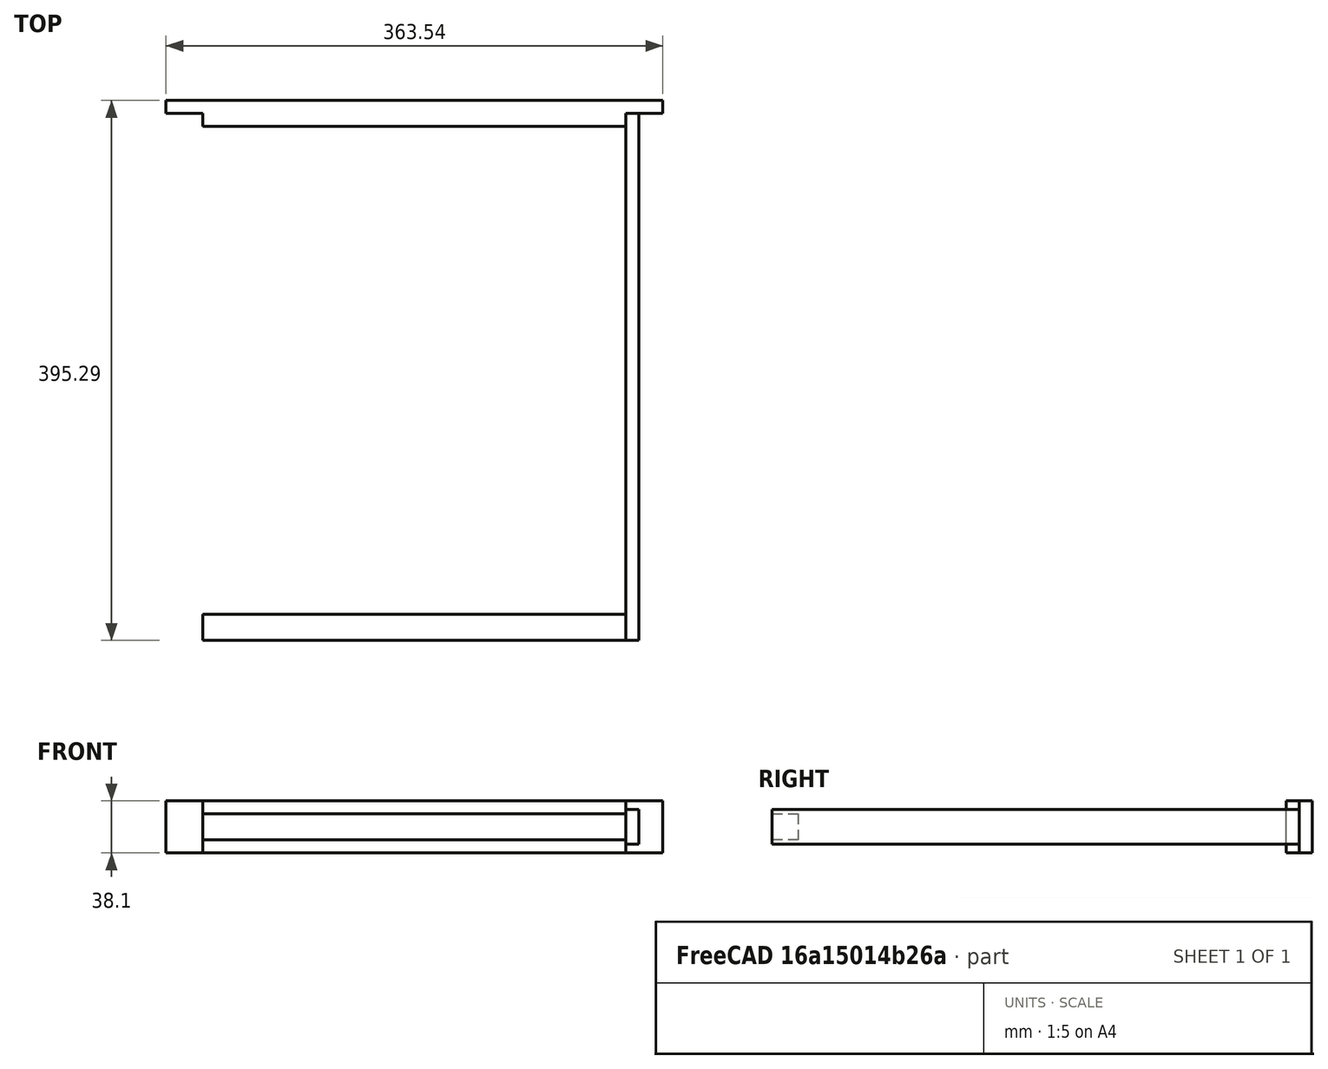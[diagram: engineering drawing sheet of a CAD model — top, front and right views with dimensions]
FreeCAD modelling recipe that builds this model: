
FCSTD DOCUMENT  (FreeCAD 0.19R24366 (Git))
Label: layens-frame
License: Creative Commons Attribution-ShareAlike
LicenseURL: http://creativecommons.org/licenses/by-sa/4.0/
objects: TechDraw::DrawViewDimension×14, TechDraw::DrawProjGroupItem×5, PartDesign::Pad×4, PartDesign::Body×4, Sketcher::SketchObject×3, PartDesign::ShapeBinder×2, App::DocumentObjectGroup×2, TechDraw::DrawSVGTemplate×1, PartDesign::FeatureBase×1, TechDraw::DrawProjGroup×1, TechDraw::DrawViewAnnotation×1, TechDraw::DrawPage×1
note: 18 computed .brp shape members not serialized (recipe doc carries the construction recipe); baked Part::Feature solids carry a one-line shape summary decoded from their .brp
EXTERNAL_REF file=layens-data.FCStd obj=Spreadsheet

FEATURE [Sketcher::SketchObject] Sketch  label="top-bar-sketch"
  FullyConstrained = true
  MapMode = 5
  Support = -> [XY_Plane]
  expr: Constraints[19] = <<layens-data>>#Spreadsheet.frame_topbar_x
  expr: Constraints[21] = <<layens-data>>#Spreadsheet.frame_topbar_z
  expr: Constraints[20] = <<layens-data>>#Spreadsheet.frame_topbar_z / 2
  sketch-geometry (8):
    g0: LineSegment StartX=-181.77 StartY=9.525 StartZ=0 EndX=-181.77 EndY=19.05 EndZ=0
    g1: LineSegment StartX=-181.77 StartY=19.05 StartZ=0 EndX=181.77 EndY=19.05 EndZ=0
    g2: LineSegment StartX=181.77 StartY=19.05 StartZ=0 EndX=181.77 EndY=9.525 EndZ=0
    g3: LineSegment StartX=181.77 StartY=9.525 StartZ=0 EndX=154.782 EndY=9.525 EndZ=0
    g4: LineSegment StartX=154.782 StartY=9.525 StartZ=0 EndX=154.782 EndY=0 EndZ=0
    g5: LineSegment StartX=154.782 StartY=0 StartZ=0 EndX=-154.782 EndY=0 EndZ=0
    g6: LineSegment StartX=-154.782 StartY=0 StartZ=0 EndX=-154.782 EndY=9.525 EndZ=0
    g7: LineSegment StartX=-154.782 StartY=9.525 StartZ=0 EndX=-181.77 EndY=9.525 EndZ=0
  constraints (23):
    c: Vertical(g0)
    c: Coincident(g0,g1)
    c: Coincident(g1,g2)
    c: Vertical(g2)
    c: Coincident(g2,g3)
    c: Horizontal(g3)
    c: Coincident(g3,g4)
    c: PointOnObject(g4,g-1)
    c: Vertical(g4)
    c: Coincident(g5,g6)
    c: Horizontal(g5)
    c: Vertical(g6)
    c: Symmetric(g0,g1,g-2)
    c: Coincident(g7,g0)
    c: Horizontal(g7)
    c: Equal(g7,g3)
    c: Coincident(g6,g7)
    c: Coincident(g5,g4)
    c: Equal(g6,g4)
    c: DistanceX(g1,g1) = 363.54
    c: DistanceY(g6,g6) = 9.525
    c: DistanceY(g5,g0) = 19.05
    c: DistanceX(g7,g7) = 26.9875
FEATURE [PartDesign::Pad] Pad  label="top-bar-pad"
  Direction = (0,0,1)
  Length = 38.1
  Length2 = 100.08
  Midplane = true
  Profile = -> Sketch
  Type = 0
  expr: Length = <<layens-data>>#Spreadsheet.frame_topbar_y
FEATURE [PartDesign::Body] Body  label="top-bar"
  Group = -> [Sketch,Pad]
  Origin = -> Origin
  Tip = -> Pad
FEATURE [PartDesign::ShapeBinder] ShapeBinder
  Support = -> [Pad]
  TraceSupport = false
FEATURE [Sketcher::SketchObject] Sketch001  label="left-bar-sketch"
  ExternalGeometry = -> [ShapeBinder]
  FullyConstrained = true
  MapMode = 5
  Placement = pos=(-154.782,0,0) rot=(0.57735,-0.57735,-0.57735;2.0944rad)
  Support = -> [ShapeBinder]
  expr: Constraints[10] = <<layens-data>>#Spreadsheet.frame_side_x
  expr: Constraints[9] = <<layens-data>>#Spreadsheet.frame_side_y
  sketch-geometry (4):
    g0: LineSegment StartX=-9.525 StartY=12.7 StartZ=0 EndX=376.235 EndY=12.7 EndZ=0
    g1: LineSegment StartX=376.235 StartY=12.7 StartZ=0 EndX=376.235 EndY=-12.7 EndZ=0
    g2: LineSegment StartX=376.235 StartY=-12.7 StartZ=0 EndX=-9.525 EndY=-12.7 EndZ=0
    g3: LineSegment StartX=-9.525 StartY=-12.7 StartZ=0 EndX=-9.525 EndY=12.7 EndZ=0
  constraints (11):
    c: Coincident(g0,g1)
    c: Coincident(g1,g2)
    c: Coincident(g2,g3)
    c: Coincident(g3,g0)
    c: Horizontal(g0)
    c: Horizontal(g2)
    c: Vertical(g1)
    c: PointOnObject(g0,g-3)
    c: Symmetric(g2,g0,g-1)
    c: DistanceX(g2,g2) = 385.76
    c: DistanceY(g3,g3) = 25.4
FEATURE [PartDesign::Pad] Pad001
  Direction = (1,1,1)
  Length = 9.525
  Length2 = 100.076
  Profile = -> Sketch001
  Type = 0
FEATURE [PartDesign::Pad] Pad002  label="left-bar-pad"
  BaseFeature = -> Pad001
  Direction = (1,1,1)
  Length = 9.53
  Length2 = 100.08
  Profile = -> Sketch001
  Type = 0
  expr: Length = <<layens-data>>#Spreadsheet.frame_side_z
FEATURE [PartDesign::Body] Body001  label="left-bar"
  Group = -> [ShapeBinder,Sketch001,Pad001,Pad002]
  Origin = -> Origin001
  Tip = -> Pad002
FEATURE [PartDesign::ShapeBinder] ShapeBinder002
  Support = -> [Pad002]
  TraceSupport = false
FEATURE [Sketcher::SketchObject] Sketch004  label="bottom-bar-sketch"
  ExternalGeometry = -> [ShapeBinder002]
  FullyConstrained = true
  MapMode = 5
  Placement = pos=(-154.782,0,0) rot=(0.57735,0.57735,0.57735;2.0944rad)
  Support = -> [ShapeBinder002]
  expr: Constraints[9] = <<layens-data>>#Spreadsheet.bottom_bar_z
  expr: Constraints[8] = <<layens-data>>#Spreadsheet.bottom_bar_y
  sketch-geometry (4):
    g0: LineSegment StartX=-376.235 StartY=9.525 StartZ=0 EndX=-357.185 EndY=9.525 EndZ=0
    g1: LineSegment StartX=-357.185 StartY=9.525 StartZ=0 EndX=-357.185 EndY=-9.525 EndZ=0
    g2: LineSegment StartX=-357.185 StartY=-9.525 StartZ=0 EndX=-376.235 EndY=-9.525 EndZ=0
    g3: LineSegment StartX=-376.235 StartY=-9.525 StartZ=0 EndX=-376.235 EndY=9.525 EndZ=0
  constraints (11):
    c: Coincident(g0,g1)
    c: Coincident(g1,g2)
    c: Coincident(g2,g3)
    c: Coincident(g3,g0)
    c: Horizontal(g0)
    c: Horizontal(g2)
    c: Vertical(g1)
    c: PointOnObject(g0,g-4)
    c: DistanceX(g0,g0) = 19.05
    c: DistanceY(g1,g1) = 19.05
    c: Symmetric(g0,g2,g-1)
FEATURE [PartDesign::Pad] Pad006  label="bottom-bar-pad"
  Direction = (1,1,1)
  Length = 309.56
  Length2 = 100.08
  Profile = -> Sketch004
  Type = 0
  expr: Length = <<layens-data>>#Spreadsheet.bottom_bar_x
FEATURE [PartDesign::Body] Body004  label="bottom-bar"
  Group = -> [ShapeBinder002,Sketch004,Pad006]
  Origin = -> Origin004
  Tip = -> Pad006
FEATURE [TechDraw::DrawSVGTemplate] Template
  EditableTexts = Designed_by_Name=T.GREENWOOD; Drawing_number=LAYENS-001; FC-Date=AUG 08, 2022; FC-SC=1:6; FC-SH=01; FC-Title=Layens Frame; Subtitle=Simplified Layens Frame; Weight=Weight
  Height = 210
  Orientation = 1
  Width = 297
FEATURE [TechDraw::DrawViewDimension] Dimension002
  Arbitrary = false
  ArbitraryTolerances = false
  EqualTolerance = true
  FormatSpec = %.1f
  FormatSpecOverTolerance = %+.1f
  FormatSpecUnderTolerance = %+.1f
  Inverted = false
  LockPosition = false
  MeasureType = 1
  OverTolerance = 0
  Rotation = 0
  ScaleType = 1
  TheoreticalExact = false
  Type = 1
  UnderTolerance = 0
  X = -0.67029
  Y = 29.7806
FEATURE [TechDraw::DrawViewDimension] Dimension003
  Arbitrary = false
  ArbitraryTolerances = false
  EqualTolerance = true
  FormatSpec = %.1f
  FormatSpecOverTolerance = %+.1f
  FormatSpecUnderTolerance = %+.1f
  Inverted = false
  LockPosition = false
  MeasureType = 1
  OverTolerance = 0
  Rotation = 0
  ScaleType = 1
  TheoreticalExact = false
  Type = 2
  UnderTolerance = 0
  X = 25.2827
  Y = 23.1248
FEATURE [TechDraw::DrawViewDimension] Dimension004
  Arbitrary = false
  ArbitraryTolerances = false
  EqualTolerance = true
  FormatSpec = %.1f
  FormatSpecOverTolerance = %+.1f
  FormatSpecUnderTolerance = %+.1f
  Inverted = false
  LockPosition = false
  MeasureType = 1
  OverTolerance = 0
  Rotation = 0
  ScaleType = 1
  TheoreticalExact = false
  Type = 2
  UnderTolerance = 0
  X = 35.072
  Y = -4.94245
FEATURE [TechDraw::DrawViewDimension] Dimension005
  Arbitrary = false
  ArbitraryTolerances = false
  EqualTolerance = true
  FormatSpec = %.1f
  FormatSpecOverTolerance = %+.1f
  FormatSpecUnderTolerance = %+.1f
  Inverted = false
  LockPosition = false
  MeasureType = 1
  OverTolerance = 0
  Rotation = 0
  ScaleType = 1
  TheoreticalExact = false
  Type = 2
  UnderTolerance = 0
  X = -21.4843
  Y = 10.4364
FEATURE [PartDesign::FeatureBase] Clone
  BaseFeature = -> Body001
FEATURE [PartDesign::Body] Body005  label="right-bar"
  BaseFeature = -> Body001
  Group = -> [Clone]
  Origin = -> Origin005
  Placement = pos=(319,0,0) rot=(0,0,1;0rad)
  Tip = -> Clone
FEATURE [App::DocumentObjectGroup] Group  label="frame-pieces"
  Group = -> [Body,Body001,Body004,Body005]
FEATURE [TechDraw::DrawProjGroupItem] ProjItem  label="Front"
  CoarseView = false
  Direction = (0,0,1)
  Focus = 100
  HardHidden = false
  IsoCount = 0
  IsoHidden = false
  IsoVisible = false
  LockPosition = true
  Perspective = false
  Rotation = 0
  RotationVector = (1,0,0)
  Scale = 0.2
  ScaleType = 2
  SeamHidden = false
  SeamVisible = true
  SmoothHidden = false
  SmoothVisible = true
  Source = -> [Group]
  Type = 0
  X = 0
  XDirection = (1,0,0)
  Y = 0
FEATURE [TechDraw::DrawProjGroupItem] ProjItem001  label="Right"
  CoarseView = false
  Direction = (1,0,1e-16)
  Focus = 100
  HardHidden = false
  IsoCount = 0
  IsoHidden = false
  IsoVisible = false
  LockPosition = true
  Perspective = false
  Rotation = 0
  RotationVector = (1,0,0)
  Scale = 0.2
  ScaleType = 2
  SeamHidden = false
  SeamVisible = true
  SmoothHidden = false
  SmoothVisible = true
  Source = -> [Group]
  Type = 2
  X = -66.506
  XDirection = (1e-16,0,-1)
  Y = 0
FEATURE [TechDraw::DrawProjGroupItem] ProjItem002  label="Top"
  CoarseView = false
  Direction = (0,1,0)
  Focus = 100
  HardHidden = false
  IsoCount = 0
  IsoHidden = false
  IsoVisible = false
  LockPosition = true
  Perspective = false
  Rotation = 0
  RotationVector = (1,0,0)
  Scale = 0.2
  ScaleType = 2
  SeamHidden = false
  SeamVisible = true
  SmoothHidden = false
  SmoothVisible = true
  Source = -> [Group]
  Type = 4
  X = 0
  XDirection = (1,0,0)
  Y = 54.7687
FEATURE [TechDraw::DrawProjGroupItem] ProjItem003  label="Bottom"
  CoarseView = false
  Direction = (0,-1,0)
  Focus = 100
  HardHidden = false
  IsoCount = 0
  IsoHidden = false
  IsoVisible = false
  LockPosition = true
  Perspective = false
  Rotation = 0
  RotationVector = (1,0,0)
  Scale = 0.2
  ScaleType = 2
  SeamHidden = false
  SeamVisible = true
  SmoothHidden = false
  SmoothVisible = true
  Source = -> [Group]
  Type = 5
  X = 0
  XDirection = (1,0,0)
  Y = -70.8211
FEATURE [TechDraw::DrawProjGroupItem] ProjItem004  label="FrontBottomLeft"
  CoarseView = false
  Direction = (-0.57735,-0.57735,0.57735)
  Focus = 100
  HardHidden = false
  IsoCount = 0
  IsoHidden = false
  IsoVisible = false
  LockPosition = true
  Perspective = false
  Rotation = 0
  RotationVector = (1,0,0)
  Scale = 0.2
  ScaleType = 2
  SeamHidden = false
  SeamVisible = true
  SmoothHidden = false
  SmoothVisible = true
  Source = -> [Group]
  Type = 8
  X = 126.678
  XDirection = (0.707107,0,0.707107)
  Y = 19.7659
FEATURE [TechDraw::DrawProjGroup] ProjGroup
  Anchor = -> ProjItem
  AutoDistribute = true
  LockPosition = true
  ProjectionType = 0
  Rotation = 0
  Scale = 0.2
  ScaleType = 2
  Source = -> [Group]
  Views = -> [ProjItem,ProjItem001,ProjItem002,ProjItem003,ProjItem004]
  X = 90.6642
  Y = 112.428
  spacingX = 15
  spacingY = 15
FEATURE [TechDraw::DrawViewDimension] Dimension
  Arbitrary = false
  ArbitraryTolerances = false
  EqualTolerance = true
  FormatSpec = %.1f
  FormatSpecOverTolerance = %+.1f
  FormatSpecUnderTolerance = %+.1f
  Inverted = false
  LockPosition = false
  MeasureType = 1
  OverTolerance = 0
  References2D = -> [ProjItem002]
  Rotation = 0
  ScaleType = 1
  TheoreticalExact = false
  Type = 1
  UnderTolerance = 0
  X = -3.41351
  Y = 13.7402
FEATURE [TechDraw::DrawViewDimension] Dimension006
  Arbitrary = false
  ArbitraryTolerances = false
  EqualTolerance = true
  FormatSpec = %.1f
  FormatSpecOverTolerance = %+.1f
  FormatSpecUnderTolerance = %+.1f
  Inverted = false
  LockPosition = false
  MeasureType = 1
  OverTolerance = 0
  References2D = -> [ProjItem]
  Rotation = 0
  ScaleType = 1
  TheoreticalExact = false
  Type = 2
  UnderTolerance = 0
  X = -47.0542
  Y = 41.4194
FEATURE [TechDraw::DrawViewDimension] Dimension007
  Arbitrary = false
  ArbitraryTolerances = false
  EqualTolerance = true
  FormatSpec = %.1f
  FormatSpecOverTolerance = %+.1f
  FormatSpecUnderTolerance = %+.1f
  Inverted = false
  LockPosition = false
  MeasureType = 1
  OverTolerance = 0
  References2D = -> [ProjItem]
  Rotation = 0
  ScaleType = 1
  TheoreticalExact = false
  Type = 2
  UnderTolerance = 0
  X = 39.4024
  Y = 30.7597
FEATURE [TechDraw::DrawViewDimension] Dimension008
  Arbitrary = false
  ArbitraryTolerances = false
  EqualTolerance = true
  FormatSpec = %.1f
  FormatSpecOverTolerance = %+.1f
  FormatSpecUnderTolerance = %+.1f
  Inverted = false
  LockPosition = false
  MeasureType = 1
  OverTolerance = 0
  References2D = -> [ProjItem]
  Rotation = 0
  ScaleType = 1
  TheoreticalExact = false
  Type = 1
  UnderTolerance = 0
  X = 1.52937
  Y = -49.685
FEATURE [TechDraw::DrawViewDimension] Dimension009
  Arbitrary = false
  ArbitraryTolerances = false
  EqualTolerance = true
  FormatSpec = %.1f
  FormatSpecOverTolerance = %+.1f
  FormatSpecUnderTolerance = %+.1f
  Inverted = false
  LockPosition = false
  MeasureType = 1
  OverTolerance = 0
  References2D = -> [ProjItem]
  Rotation = 0
  ScaleType = 1
  TheoreticalExact = false
  Type = 1
  UnderTolerance = 0
  X = 38.973
  Y = -43.2112
FEATURE [TechDraw::DrawViewDimension] Dimension010
  Arbitrary = false
  ArbitraryTolerances = false
  EqualTolerance = true
  FormatSpec = %.1f
  FormatSpecOverTolerance = %+.1f
  FormatSpecUnderTolerance = %+.1f
  Inverted = false
  LockPosition = false
  MeasureType = 1
  OverTolerance = 0
  References2D = -> [ProjItem]
  Rotation = 0
  ScaleType = 1
  TheoreticalExact = false
  Type = 1
  UnderTolerance = 0
  X = -38.1417
  Y = -42.503
FEATURE [TechDraw::DrawViewDimension] Dimension011
  Arbitrary = false
  ArbitraryTolerances = false
  EqualTolerance = true
  FormatSpec = %.1f
  FormatSpecOverTolerance = %+.1f
  FormatSpecUnderTolerance = %+.1f
  Inverted = false
  LockPosition = false
  MeasureType = 1
  OverTolerance = 0
  References2D = -> [ProjItem001]
  Rotation = 0
  ScaleType = 1
  TheoreticalExact = false
  Type = 1
  UnderTolerance = 0
  X = -0.236068
  Y = 50.0335
FEATURE [TechDraw::DrawViewDimension] Dimension012
  Arbitrary = false
  ArbitraryTolerances = false
  EqualTolerance = true
  FormatSpec = %.1f
  FormatSpecOverTolerance = %+.1f
  FormatSpecUnderTolerance = %+.1f
  Inverted = false
  LockPosition = false
  MeasureType = 1
  OverTolerance = 0
  References2D = -> [ProjItem001]
  Rotation = 0
  ScaleType = 1
  TheoreticalExact = false
  Type = 1
  UnderTolerance = 0
  X = 0
  Y = -43.1998
FEATURE [TechDraw::DrawViewDimension] Dimension013
  Arbitrary = false
  ArbitraryTolerances = false
  EqualTolerance = true
  FormatSpec = %.1f
  FormatSpecOverTolerance = %+.1f
  FormatSpecUnderTolerance = %+.1f
  Inverted = false
  LockPosition = false
  MeasureType = 1
  OverTolerance = 0
  References2D = -> [ProjItem003]
  Rotation = 0
  ScaleType = 1
  TheoreticalExact = false
  Type = 2
  UnderTolerance = 0
  X = -48.2863
  Y = 1.61625
FEATURE [TechDraw::DrawViewDimension] Dimension014
  Arbitrary = false
  ArbitraryTolerances = false
  EqualTolerance = true
  FormatSpec = %.1f
  FormatSpecOverTolerance = %+.1f
  FormatSpecUnderTolerance = %+.1f
  Inverted = false
  LockPosition = false
  MeasureType = 1
  OverTolerance = 0
  References2D = -> [ProjItem]
  Rotation = 0
  ScaleType = 1
  TheoreticalExact = false
  Type = 2
  UnderTolerance = 0
  X = 44.6373
  Y = -27.383
FEATURE [TechDraw::DrawViewAnnotation] Annotation
  Font = osifont
  LineSpace = 80
  LockPosition = true
  MaxWidth = -1
  Rotation = 0
  ScaleType = 1
  Text = millimeters
  TextSize = 5
  TextStyle = 0
  X = 205.5
  Y = 33
FEATURE [TechDraw::DrawPage] Page  label="layens-frame"
  KeepUpdated = true
  NextBalloonIndex = 1
  ProjectionType = 0
  Template = -> Template
  Views = -> [Dimension002,Dimension003,Dimension004,Dimension005,ProjGroup,Dimension,Dimension006,Dimension007,Dimension008,Dimension009,Dimension010,Dimension011,Dimension012,Dimension013,Dimension014,Annotation]
FEATURE [App::DocumentObjectGroup] Group001  label="drawings"
  Group = -> [Page]
